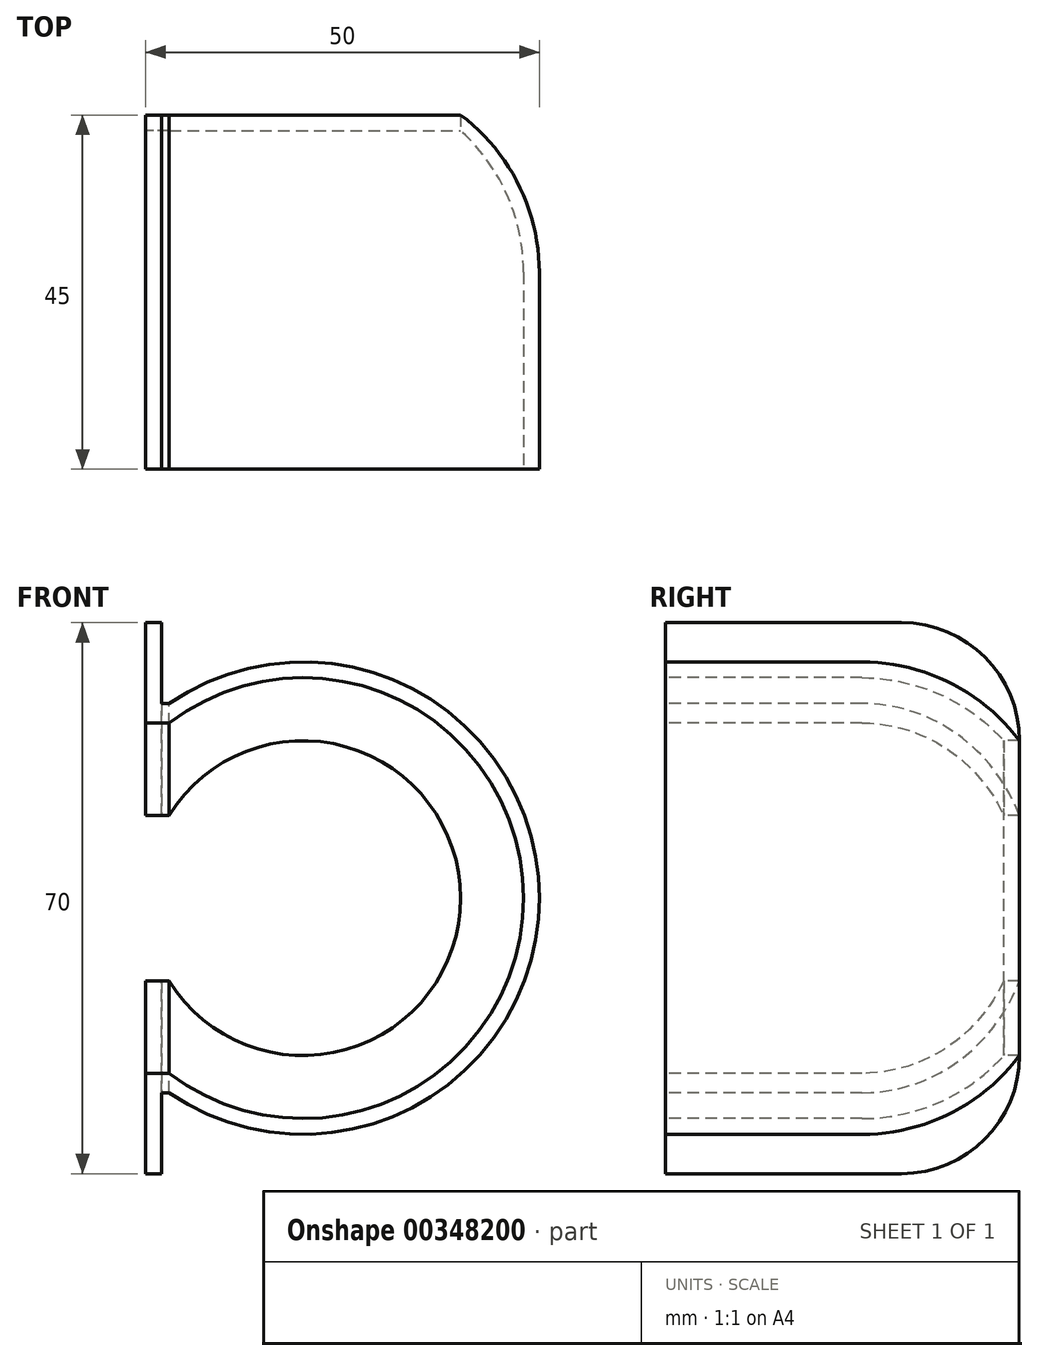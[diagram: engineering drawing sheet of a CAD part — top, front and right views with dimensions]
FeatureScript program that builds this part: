
annotation { "Feature Type Name" : "Feature", "Feature Type Description" : "" }
export const myFeature = defineFeature(function(context is Context, id is Id, definition is map)
    precondition{}
    {
        {
            var Q0;
            Q0=qCreatedBy(makeId("Top.planeOp"),FACE);
            var sketch = newSketch(context, id + "F0", { "sketchPlane" : qUnion([Q0])});
            skLineSegment(sketch, "E0", {"start": v(0, 0) * mm, "end": v(30, 0) * mm});
            skLineSegment(sketch, "E1", {"start": v(30, 0) * mm, "end": v(30, 45) * mm});
            skLineSegment(sketch, "E2", {"start": v(0, 0) * mm, "end": v(0, 25) * mm});
            skArc(sketch, "E3", {"start": v(10, 45) * mm, "mid": v(2.64, 36.18) * mm, "end": v(0, 25) * mm});
            skLineSegment(sketch, "E4", {"start": v(10, 45) * mm, "end": v(10, 43) * mm});
            skLineSegment(sketch, "E5", {"start": v(0, 0) * mm, "end": v(2, 0) * mm});
            skLineSegment(sketch, "E6", {"start": v(2, 0) * mm, "end": v(2, 25) * mm});
            skArc(sketch, "E7", {"start": v(10, 43) * mm, "mid": v(4.1, 34.85) * mm, "end": v(2, 25) * mm});
            skSolve(sketch);
        }
        {
            var Q0;
            Q0=makeQuery(id+"F0.imprint","IMPRINT",FACE,{"disambiguationData":[TD([[makeQuery(id+"F0.imprint","IMPRINT",EDGE,{"derivedFrom":sQuery(id+"F0.wireOp",EDGE,"E2")}),-1.0]])]});
            var Q1;
            Q1=sQuery(id+"F0.wireOp",EDGE,"E1");
            revolve(context, id + "F1", {"entities" : qUnion([Q0]), "axis" : qUnion([Q1]), "revolveType" : RevolveType.FULL});
        }
        {
            var Q0;
            Q0=qCreatedBy(makeId("Right.planeOp"),FACE);
            var sketch = newSketch(context, id + "F2", { "sketchPlane" : qUnion([Q0])});
            skLineSegment(sketch, "E8", {"start": v(0, 0) * mm, "end": v(0, -30) * mm});
            skLineSegment(sketch, "E9", {"start": v(0, -30) * mm, "end": v(45, -30) * mm});
            skLineSegment(sketch, "E10", {"start": v(45, -30) * mm, "end": v(45, 30) * mm});
            skLineSegment(sketch, "E11", {"start": v(45, 30) * mm, "end": v(0, 30) * mm});
            skLineSegment(sketch, "E12", {"start": v(0, 30) * mm, "end": v(0, 0) * mm});
            skSolve(sketch);
        }
        {
            var Q0;
            Q0=makeQuery(id+"F2.imprint","IMPRINT",FACE,{"disambiguationData":[TD([[makeQuery(id+"F2.imprint","IMPRINT",EDGE,{"derivedFrom":sQuery(id+"F2.wireOp",EDGE,"E8")}),1.0]])]});
            extrude(context, id + "F3", {"entities" : qUnion([Q0]), "operationType" : NewBodyOperationType.ADD, "depth" : 13 * mm, "offsetDistance" : 25 * mm});
        }
        {
            var Q0;
            Q0=makeQuery(id+"F3.opExtrude","SWEPT_FACE",FACE,{"disambiguationData":[OSD([sQuery(id+"F2.wireOp",EDGE,"E11")])]});
            extrude(context, id + "F4", {"entities" : qUnion([Q0]), "operationType" : NewBodyOperationType.ADD, "depth" : 5 * mm, "offsetDistance" : 25 * mm});
        }
        {
            var Q0;
            Q0=makeQuery(id+"F3.opExtrude","SWEPT_FACE",FACE,{"disambiguationData":[OSD([sQuery(id+"F2.wireOp",EDGE,"E9")])]});
            extrude(context, id + "F5", {"entities" : qUnion([Q0]), "operationType" : NewBodyOperationType.ADD, "depth" : 5 * mm, "offsetDistance" : 25 * mm});
        }
        {
            var Q0;
            {var subQ0=sQuery(id+"F2.wireOp",EDGE,"E9");var subQ1=sQuery(id+"F2.wireOp",EDGE,"E11");Q0=makeQuery(id+"F5.boolean.opBoolean","MERGE",FACE,{"derivedFrom":[makeQuery(id+"F4.boolean.opBoolean","MERGE",FACE,{"derivedFrom":[makeQuery(id+"F3.opExtrude","CAP_FACE",FACE,{"disambiguationData":[OSD([sQuery(id+"F2.wireOp",EDGE,"E8"),subQ0,sQuery(id+"F2.wireOp",EDGE,"E10"),subQ1,sQuery(id+"F2.wireOp",EDGE,"E12")])],"isStart":true}),makeQuery(id+"F4.opExtrude","SWEPT_FACE",FACE,{"disambiguationData":[OSD([subQ1]),TDD([makeQuery(id+"F3.opExtrude","CAP_EDGE",EDGE,{"disambiguationData":[OSD([subQ1])],"isStart":true})])]})]}),makeQuery(id+"F5.opExtrude","SWEPT_FACE",FACE,{"disambiguationData":[OSD([subQ0]),TDD([makeQuery(id+"F3.opExtrude","CAP_EDGE",EDGE,{"disambiguationData":[OSD([subQ0])],"isStart":true})])]})]});}
            extrude(context, id + "F6", {"entities" : qUnion([Q0]), "operationType" : NewBodyOperationType.REMOVE, "oppositeDirection" : true, "depth" : 11 * mm, "offsetDistance" : 25 * mm});
        }
        {
            var Q0;
            {var subQ0=sQuery(id+"F2.wireOp",EDGE,"E12");var subQ1=sQuery(id+"F2.wireOp",EDGE,"E8");var subQ2=sQuery(id+"F2.wireOp",EDGE,"E10");var subQ3=makeQuery(id+"F3.opExtrude","CAP_FACE",FACE,{"disambiguationData":[OSD([subQ1,sQuery(id+"F2.wireOp",EDGE,"E9"),subQ2,sQuery(id+"F2.wireOp",EDGE,"E11"),subQ0])],"isStart":false});Q0=makeQuery(id+"F3.boolean.opBoolean","SPLIT",FACE,{"disambiguationData":[TD([makeQuery(id+"F1.opRevolve","SWEPT_FACE",FACE,{"disambiguationData":[OSD([sQuery(id+"F0.wireOp",EDGE,"E6")])]})])],"derivedFrom":subQ3});}
            extrude(context, id + "F7", {"entities" : qUnion([Q0]), "operationType" : NewBodyOperationType.REMOVE, "oppositeDirection" : true, "depth" : 25 * mm, "offsetDistance" : 25 * mm});
        }
        {
            var Q0;
            {var subQ0=sQuery(id+"F2.wireOp",EDGE,"E12");var subQ1=sQuery(id+"F2.wireOp",EDGE,"E11");var subQ2=sQuery(id+"F2.wireOp",EDGE,"E10");var subQ3=sQuery(id+"F2.wireOp",EDGE,"E9");var subQ4=sQuery(id+"F2.wireOp",EDGE,"E8");Q0=makeQuery(id+"F7.boolean.opBoolean","SPLIT",FACE,{"disambiguationData":[TD([makeQuery(id+"F5.opExtrude","CAP_FACE",FACE,{"disambiguationData":[OSD([subQ3])],"isStart":false})])],"derivedFrom":makeQuery(id+"F6.boolean.opBoolean","COPY",FACE,{"derivedFrom":makeQuery(id+"F6.opExtrude","CAP_FACE",FACE,{"disambiguationData":[OSD([subQ4,subQ3,subQ2,subQ1,subQ0])],"isStart":false})})});}
            var Q1;
            {var subQ0=sQuery(id+"F2.wireOp",EDGE,"E10");var subQ1=sQuery(id+"F2.wireOp",EDGE,"E9");var subQ2=sQuery(id+"F2.wireOp",EDGE,"E8");var subQ3=sQuery(id+"F2.wireOp",EDGE,"E12");var subQ4=sQuery(id+"F2.wireOp",EDGE,"E11");Q1=makeQuery(id+"F7.boolean.opBoolean","SPLIT",FACE,{"disambiguationData":[TD([makeQuery(id+"F4.opExtrude","CAP_FACE",FACE,{"disambiguationData":[OSD([subQ4])],"isStart":false})])],"derivedFrom":makeQuery(id+"F6.boolean.opBoolean","COPY",FACE,{"derivedFrom":makeQuery(id+"F6.opExtrude","CAP_FACE",FACE,{"disambiguationData":[OSD([subQ2,subQ1,subQ0,subQ4,subQ3])],"isStart":false})})});}
            extrude(context, id + "F8", {"entities" : qUnion([Q0, Q1]), "operationType" : NewBodyOperationType.ADD, "depth" : 1 * mm, "offsetDistance" : 25 * mm});
        }
        {
            var Q0;
            {var subQ0=sQuery(id+"F2.wireOp",EDGE,"E11");var subQ1=sQuery(id+"F2.wireOp",EDGE,"E12");var subQ2=sQuery(id+"F2.wireOp",EDGE,"E8");var subQ3=sQuery(id+"F2.wireOp",EDGE,"E10");var subQ4=makeQuery(id+"F3.opExtrude","CAP_FACE",FACE,{"disambiguationData":[OSD([subQ2,sQuery(id+"F2.wireOp",EDGE,"E9"),subQ3,subQ0,subQ1])],"isStart":false});Q0=makeQuery(id+"F4.boolean.opBoolean","MERGE",FACE,{"derivedFrom":[makeQuery(id+"F3.boolean.opBoolean","SPLIT",FACE,{"disambiguationData":[TD([makeQuery(id+"F3.opExtrude","SWEPT_FACE",FACE,{"disambiguationData":[OSD([subQ0])]})])],"derivedFrom":subQ4}),makeQuery(id+"F4.opExtrude","SWEPT_FACE",FACE,{"disambiguationData":[OSD([subQ0]),TDD([makeQuery(id+"F3.opExtrude","CAP_EDGE",EDGE,{"disambiguationData":[OSD([subQ0])],"isStart":false})])]})]});}
            var Q1;
            {var subQ0=sQuery(id+"F2.wireOp",EDGE,"E9");var subQ1=sQuery(id+"F2.wireOp",EDGE,"E12");var subQ2=sQuery(id+"F2.wireOp",EDGE,"E8");var subQ3=sQuery(id+"F2.wireOp",EDGE,"E10");var subQ4=makeQuery(id+"F3.opExtrude","CAP_FACE",FACE,{"disambiguationData":[OSD([subQ2,subQ0,subQ3,sQuery(id+"F2.wireOp",EDGE,"E11"),subQ1])],"isStart":false});Q1=makeQuery(id+"F5.boolean.opBoolean","MERGE",FACE,{"derivedFrom":[makeQuery(id+"F3.boolean.opBoolean","SPLIT",FACE,{"disambiguationData":[TD([makeQuery(id+"F3.opExtrude","SWEPT_FACE",FACE,{"disambiguationData":[OSD([subQ0])]})])],"derivedFrom":subQ4}),makeQuery(id+"F5.opExtrude","SWEPT_FACE",FACE,{"disambiguationData":[OSD([subQ0]),TDD([makeQuery(id+"F3.opExtrude","CAP_EDGE",EDGE,{"disambiguationData":[OSD([subQ0])],"isStart":false})])]})]});}
            extrude(context, id + "F9", {"entities" : qUnion([Q0, Q1]), "operationType" : NewBodyOperationType.REMOVE, "oppositeDirection" : true, "depth" : 1 * mm, "offsetDistance" : 25 * mm});
        }
        {
            var Q0;
            {var subQ0=sQuery(id+"F2.wireOp",EDGE,"E11");var subQ1=sQuery(id+"F2.wireOp",EDGE,"E10");Q0=makeQuery(id+"F8.boolean.opBoolean","MERGE",EDGE,{"derivedFrom":[makeQuery(id+"F4.opExtrude","CAP_EDGE",EDGE,{"disambiguationData":[OSD([subQ1,subQ0])],"isStart":false}),makeQuery(id+"F8.opExtrude","SWEPT_EDGE",EDGE,{"disambiguationData":[OSD([subQ1,subQ0])]})]});}
            var Q1;
            {var subQ0=sQuery(id+"F2.wireOp",EDGE,"E10");var subQ1=sQuery(id+"F2.wireOp",EDGE,"E9");Q1=makeQuery(id+"F8.boolean.opBoolean","MERGE",EDGE,{"derivedFrom":[makeQuery(id+"F5.opExtrude","CAP_EDGE",EDGE,{"disambiguationData":[OSD([subQ1,subQ0])],"isStart":false}),makeQuery(id+"F8.opExtrude","SWEPT_EDGE",EDGE,{"disambiguationData":[OSD([subQ1,subQ0])]})]});}
            fillet(context, id + "F10", {"entities" : qUnion([Q0, Q1]), "radius" : 15 * mm, "tangentPropagation" : true, "allowEdgeOverflow" : false});
        }
    });
